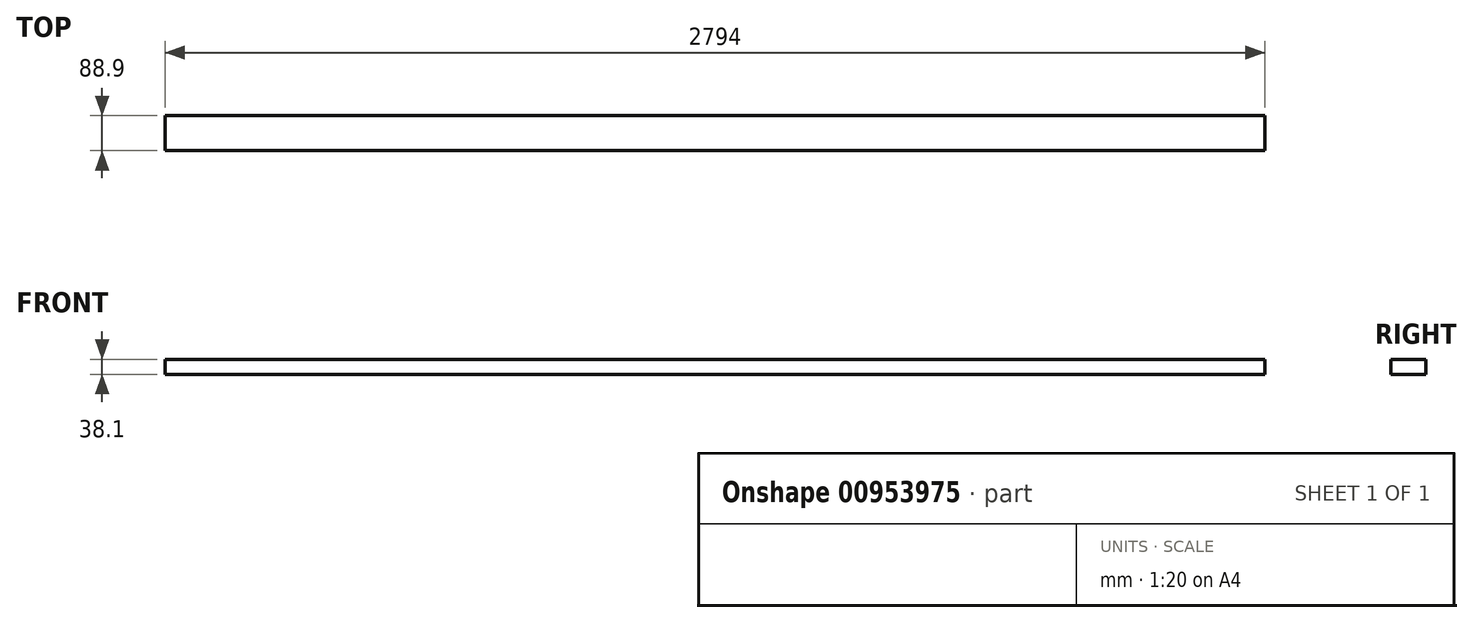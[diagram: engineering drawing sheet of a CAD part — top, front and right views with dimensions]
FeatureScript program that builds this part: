
annotation { "Feature Type Name" : "Feature", "Feature Type Description" : "" }
export const myFeature = defineFeature(function(context is Context, id is Id, definition is map)
    precondition{}
    {
        {
            var Q0;
            Q0=qCreatedBy(makeId("Right.planeOp"),FACE);
            var sketch = newSketch(context, id + "F0", { "sketchPlane" : qUnion([Q0])});
            skLineSegment(sketch, "E0.bottom", {"start": v(44.45, 19.05) * mm, "end": v(-44.45, 19.05) * mm});
            skLineSegment(sketch, "E0.top", {"start": v(44.45, -19.05) * mm, "end": v(-44.45, -19.05) * mm});
            skLineSegment(sketch, "E0.left", {"start": v(44.45, 19.05) * mm, "end": v(44.45, -19.05) * mm});
            skLineSegment(sketch, "E0.right", {"start": v(-44.45, 19.05) * mm, "end": v(-44.45, -19.05) * mm});
            skPoint(sketch, "E0.middle", {"position": v(0, 0) * mm});
            skSolve(sketch);
        }
        {
            var Q0;
            Q0=qSketchRegion(id+"F0",true);
            extrude(context, id + "F1", {"entities" : qUnion([Q0]), "oppositeDirection" : true, "depth" : 2794 * mm, "offsetDistance" : 25.4 * mm});
        }
    });
